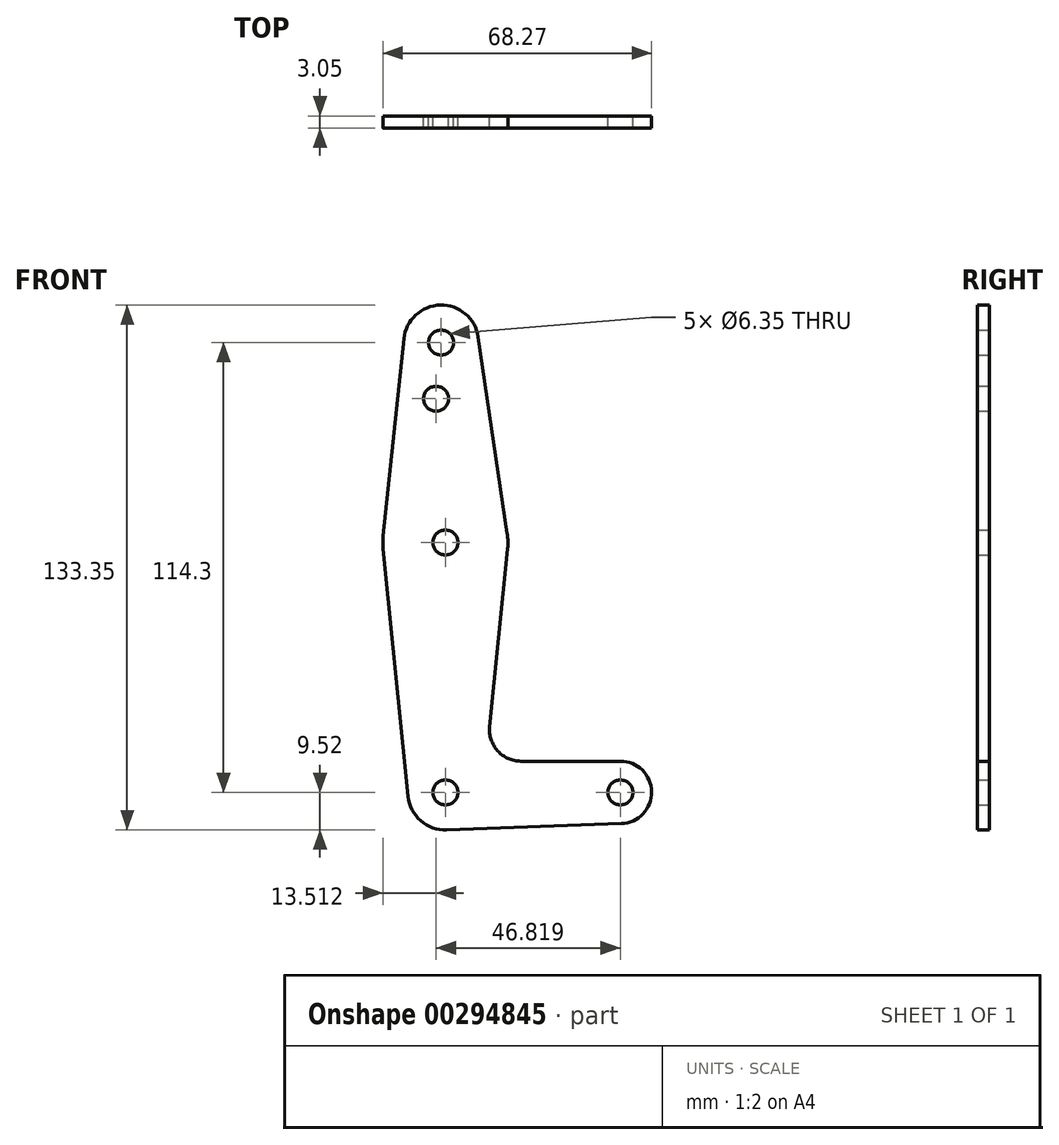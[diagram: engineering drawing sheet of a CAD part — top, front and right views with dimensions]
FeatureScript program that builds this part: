
annotation { "Feature Type Name" : "Feature", "Feature Type Description" : "" }
export const myFeature = defineFeature(function(context is Context, id is Id, definition is map)
    precondition{}
    {
        {
            var Q0;
            Q0=qCreatedBy(makeId("Front.planeOp"),FACE);
            var sketch = newSketch(context, id + "F0", { "sketchPlane" : qUnion([Q0])});
            skLineSegment(sketch, "E0", {"start": v(0, 0) * mm, "end": v(44.45, 0) * mm, "construction": true});
            skCircle(sketch, "E1", {"center": v(44.45, 0) * mm, "radius": 7.94 * mm});
            skCircle(sketch, "E2", {"center": v(-1.09, 114.3) * mm, "radius": 9.53 * mm});
            skCircle(sketch, "E3", {"center": v(0, 63.5) * mm, "radius": 15.88 * mm});
            skCircle(sketch, "E4", {"center": v(0, 0) * mm, "radius": 9.53 * mm});
            skLineSegment(sketch, "E5", {"start": v(-1.09, 114.3) * mm, "end": v(0, 63.5) * mm, "construction": true});
            skLineSegment(sketch, "E6", {"start": v(0, 63.5) * mm, "end": v(0, 0) * mm, "construction": true});
            skLineSegment(sketch, "E7", {"start": v(-10.56, 115.29) * mm, "end": v(-15.79, 65.15) * mm});
            skLineSegment(sketch, "E8", {"start": v(15.8, 61.91) * mm, "end": v(11.25, 16.68) * mm});
            skLineSegment(sketch, "E9", {"start": v(-15.8, 61.91) * mm, "end": v(-9.48, -0.95) * mm});
            skCircle(sketch, "E10", {"center": v(-1.09, 114.3) * mm, "radius": 3.18 * mm});
            skCircle(sketch, "E11", {"center": v(-2.37, 100.03) * mm, "radius": 3.18 * mm});
            skLineSegment(sketch, "E12", {"start": v(44.45, 7.94) * mm, "end": v(19.16, 7.94) * mm});
            skLineSegment(sketch, "E13", {"start": v(0.34, -9.52) * mm, "end": v(44.73, -7.93) * mm});
            skCircle(sketch, "E14", {"center": v(0, 63.5) * mm, "radius": 3.18 * mm});
            skCircle(sketch, "E15", {"center": v(0, 0) * mm, "radius": 3.18 * mm});
            skCircle(sketch, "E16", {"center": v(44.45, 0) * mm, "radius": 3.18 * mm});
            skArc(sketch, "E17.filletArc", {"start": v(11.25, 16.68) * mm, "mid": v(13.26, 10.55) * mm, "end": v(19.16, 7.94) * mm});
            skLineSegment(sketch, "E18", {"start": v(8.34, 115.7) * mm, "end": v(15.7, 65.82) * mm});
            skSolve(sketch);
        }
        {
            var Q0;
            Q0=makeQuery(id+"F0.imprint","IMPRINT",FACE,{"disambiguationData":[TD([[makeQuery(id+"F0.imprint","IMPRINT",EDGE,{"derivedFrom":sQuery(id+"F0.wireOp",EDGE,"E10")}),-1.0]])]});
            var Q1;
            {var subQ0=sQuery(id+"F0.wireOp",EDGE,"E7");Q1=makeQuery(id+"F0.imprint","IMPRINT",FACE,{"disambiguationData":[TD([[makeQuery(id+"F0.imprint","IMPRINT",EDGE,{"derivedFrom":subQ0}),1.0]])]});}
            var Q2;
            Q2=makeQuery(id+"F0.imprint","IMPRINT",FACE,{"disambiguationData":[TD([[makeQuery(id+"F0.imprint","IMPRINT",EDGE,{"derivedFrom":sQuery(id+"F0.wireOp",EDGE,"E14")}),-1.0]])]});
            var Q3;
            {var subQ0=sQuery(id+"F0.wireOp",EDGE,"E8");Q3=makeQuery(id+"F0.imprint","IMPRINT",FACE,{"disambiguationData":[TD([[makeQuery(id+"F0.imprint","IMPRINT",EDGE,{"derivedFrom":subQ0}),-1.0]])]});}
            var Q4;
            Q4=makeQuery(id+"F0.imprint","IMPRINT",FACE,{"disambiguationData":[TD([[makeQuery(id+"F0.imprint","IMPRINT",EDGE,{"derivedFrom":sQuery(id+"F0.wireOp",EDGE,"E15")}),-1.0]])]});
            var Q5;
            Q5=makeQuery(id+"F0.imprint","IMPRINT",FACE,{"disambiguationData":[TD([[makeQuery(id+"F0.imprint","IMPRINT",EDGE,{"derivedFrom":sQuery(id+"F0.wireOp",EDGE,"E16")}),-1.0]])]});
            extrude(context, id + "F1", {"entities" : qUnion([Q0, Q1, Q2, Q3, Q4, Q5]), "depth" : 3.05 * mm});
        }
    });
